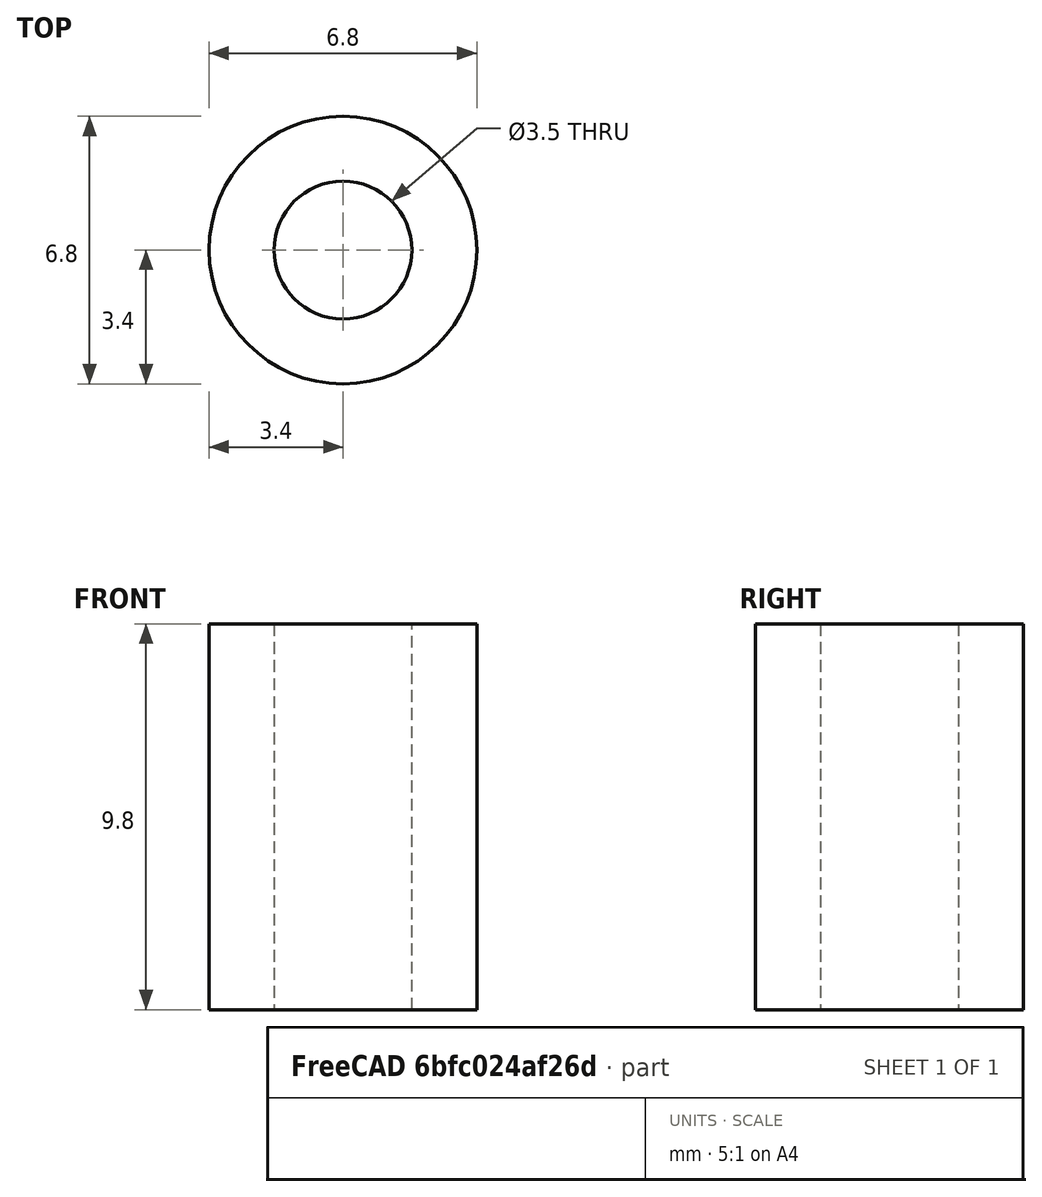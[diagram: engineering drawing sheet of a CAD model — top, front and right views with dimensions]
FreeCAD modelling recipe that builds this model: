
FCSTD DOCUMENT  (FreeCAD 0.17R13513 (Git))
Label: spacer
License: All rights reserved
LicenseURL: http://en.wikipedia.org/wiki/All_rights_reserved
objects: Sketcher::SketchObject×1, PartDesign::Pad×1, PartDesign::Body×1
note: 4 computed .brp shape members not serialized (recipe doc carries the construction recipe); baked Part::Feature solids carry a one-line shape summary decoded from their .brp

FEATURE [Sketcher::SketchObject] Sketch
  MapMode = 5
  Support = -> [XY_Plane]
  sketch-geometry (2):
    g0: Circle CenterX=0 CenterY=0 CenterZ=0 NormalX=0 NormalY=0 NormalZ=1 AngleXU=0 Radius=1.75
    g1: Circle CenterX=0 CenterY=0 CenterZ=0 NormalX=0 NormalY=0 NormalZ=1 AngleXU=0 Radius=3.4
  constraints (4):
    c: Coincident(g0,g-1)
    c: Coincident(g1,g-1)
    c: Radius(g0) = 1.75
    c: Radius(g1) = 3.4
FEATURE [PartDesign::Pad] Pad
  Length = 9.8
  Length2 = 100
  Profile = -> Sketch
  Type = 0
FEATURE [PartDesign::Body] Body
  Group = -> [Sketch,Pad]
  Origin = -> Origin
  Tip = -> Pad
